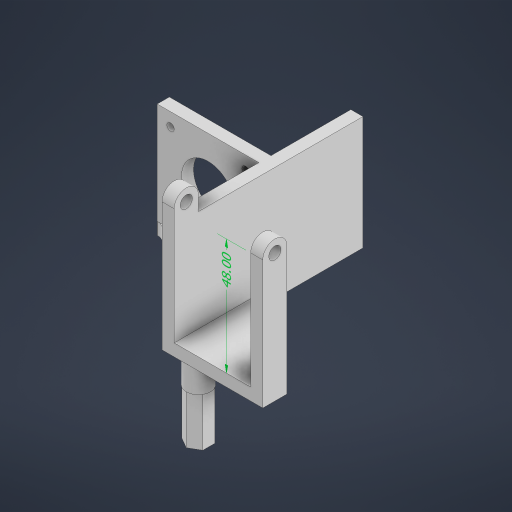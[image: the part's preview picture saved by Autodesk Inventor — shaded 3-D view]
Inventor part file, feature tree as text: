
AUTODESK INVENTOR PART (.ipt)
format: ipt  version: 2024 (Build 280153000, 153)  size: 490,496 bytes
history: native  units: mm
features: extrude x9, sketch x9, other x4, chamfer x2, fillet x1
ambient origin geometry x8: Origin, YZ Plane, XZ Plane, XY Plane, X Axis, Y Axis, Z Axis, Center Point
bodies: Body1 (feature_tree)
feature tree (25):
  other  "솔리드1"
  extrude  "돌출1"  Depth=5.0mm
  extrude  "돌출2"  Depth=10.0mm
  extrude  "돌출3"  Depth=53.0mm
  extrude  "돌출4"  Depth=10.0mm
  extrude  "돌출5"  Depth=5.0mm TaperAngle=0.0deg
  chamfer  "모따기1"  Distance=10.0mm
  extrude  "돌출6"  Depth=5.0mm
  extrude  "돌출7"  Depth=31.6mm TaperAngle=0.0deg
  extrude  "돌출8"  Depth=10.0mm
  other  "직접 편집1"
  fillet  "모깎기1"  Radius=53.0mm
  extrude  "돌출9"  Depth=5.0mm
  chamfer  "모따기2"  Distance=5.0mm
  sketch  "스케치1"
  sketch  "스케치2"
  sketch  "스케치3"
  sketch  "스케치4"
  sketch  "스케치5"
  sketch  "스케치6"
  sketch  "스케치7"
  sketch  "스케치8"
  sketch  "스케치9"
  other  "이동1"
  other  "선형 치수 1"
